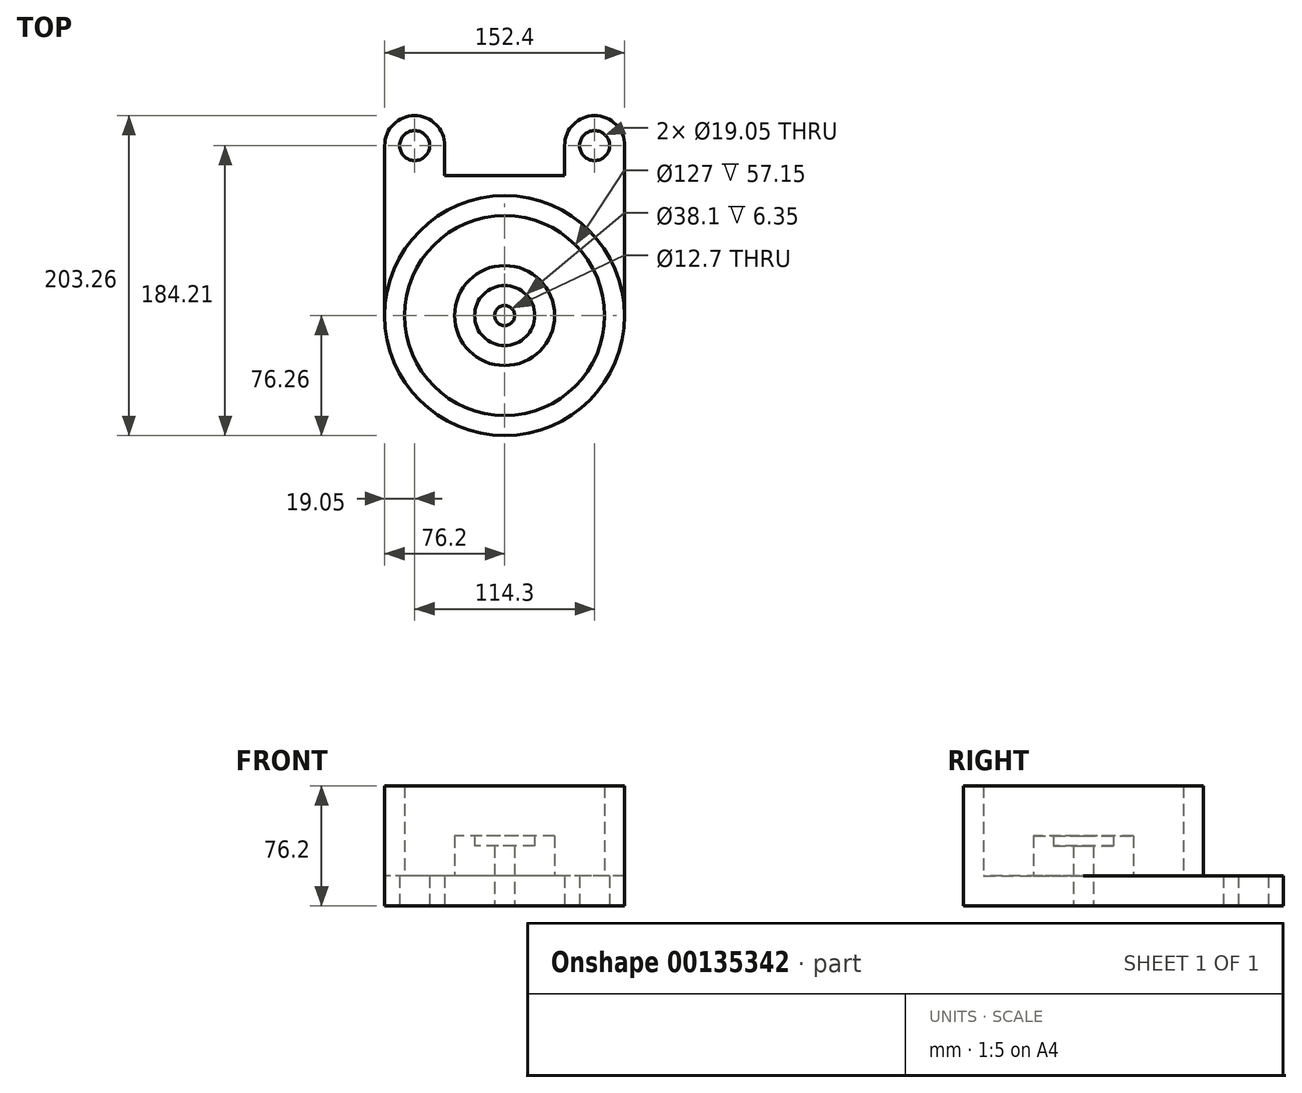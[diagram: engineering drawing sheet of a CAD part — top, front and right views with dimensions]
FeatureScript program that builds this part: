
annotation { "Feature Type Name" : "Feature", "Feature Type Description" : "" }
export const myFeature = defineFeature(function(context is Context, id is Id, definition is map)
    precondition{}
    {
        {
            var Q0;
            Q0=qCreatedBy(makeId("Top.planeOp"),FACE);
            var sketch = newSketch(context, id + "F0", { "sketchPlane" : qUnion([Q0])});
            skLineSegment(sketch, "E0", {"start": v(-76.2, 0) * mm, "end": v(0, 0) * mm, "construction": true});
            skLineSegment(sketch, "E1", {"start": v(-76.2, 0) * mm, "end": v(-76.2, 107.95) * mm});
            skArc(sketch, "E2", {"start": v(-38.1, 107.95) * mm, "mid": v(-57.15, 127) * mm, "end": v(-76.2, 107.95) * mm});
            skCircle(sketch, "E3", {"center": v(-57.15, 107.95) * mm, "radius": 9.53 * mm});
            skCircle(sketch, "E4", {"center": v(0, 0) * mm, "radius": 19.05 * mm});
            skCircle(sketch, "E5", {"center": v(0, 0) * mm, "radius": 31.75 * mm});
            skCircle(sketch, "E6", {"center": v(0, 0) * mm, "radius": 63.5 * mm});
            skCircle(sketch, "E7", {"center": v(0, -0.06) * mm, "radius": 76.2 * mm});
            skLineSegment(sketch, "E8.MirrorCS", {"start": v(-76.2, 0) * mm, "end": v(-152.4, 0) * mm, "construction": true});
            skLineSegment(sketch, "E9.MirrorCS", {"start": v(-76.2, 0) * mm, "end": v(-76.2, -107.95) * mm});
            skArc(sketch, "E10.MirrorCS", {"start": v(-38.1, -107.95) * mm, "mid": v(-57.15, -127) * mm, "end": v(-76.2, -107.95) * mm});
            skCircle(sketch, "E11.MirrorC", {"center": v(-57.15, -107.95) * mm, "radius": 9.53 * mm});
            skLineSegment(sketch, "E12", {"start": v(0, 157.5) * mm, "end": v(0, -133.46) * mm, "construction": true});
            skArc(sketch, "E13.MirrorCS", {"start": v(38.1, 107.95) * mm, "mid": v(57.15, 127) * mm, "end": v(76.2, 107.95) * mm});
            skLineSegment(sketch, "E14.MirrorCS", {"start": v(76.2, 0) * mm, "end": v(76.2, 107.95) * mm});
            skCircle(sketch, "E15.MirrorC", {"center": v(57.15, 107.95) * mm, "radius": 9.53 * mm});
            skLineSegment(sketch, "E16.MirrorCS", {"start": v(76.2, 0) * mm, "end": v(76.2, -107.95) * mm});
            skArc(sketch, "E17.MirrorCS", {"start": v(38.1, -107.95) * mm, "mid": v(57.15, -127) * mm, "end": v(76.2, -107.95) * mm});
            skCircle(sketch, "E18.MirrorC", {"center": v(57.15, -107.95) * mm, "radius": 9.53 * mm});
            skLineSegment(sketch, "E19", {"start": v(-38.1, 107.95) * mm, "end": v(-38.1, 88.9) * mm});
            skLineSegment(sketch, "E20", {"start": v(38.1, 107.95) * mm, "end": v(38.1, 88.9) * mm});
            skLineSegment(sketch, "E21", {"start": v(38.1, 88.9) * mm, "end": v(-38.1, 88.9) * mm});
            skLineSegment(sketch, "E22", {"start": v(38.1, -107.95) * mm, "end": v(38.1, -88.9) * mm});
            skLineSegment(sketch, "E23", {"start": v(38.1, -88.9) * mm, "end": v(-37.76, -88.9) * mm});
            skLineSegment(sketch, "E24", {"start": v(-37.76, -88.9) * mm, "end": v(-38.1, -107.95) * mm});
            skCircle(sketch, "E25", {"center": v(0, 0) * mm, "radius": 6.35 * mm});
            skSolve(sketch);
        }
        {
            var Q0;
            {var subQ5=sQuery(id+"F0.wireOp",EDGE,"E1");Q0=makeQuery(id+"F0.imprint","IMPRINT",FACE,{"disambiguationData":[TD([[makeQuery(id+"F0.imprint","IMPRINT",EDGE,{"derivedFrom":subQ5}),-1.0]])]});}
            var Q1;
            {var subQ0=sQuery(id+"F0.wireOp",EDGE,"E10.MirrorCS");Q1=makeQuery(id+"F0.imprint","IMPRINT",FACE,{"disambiguationData":[TD([[makeQuery(id+"F0.imprint","IMPRINT",EDGE,{"derivedFrom":subQ0}),-1.0]])]});}
            var Q2;
            Q2=makeQuery(id+"F0.imprint","IMPRINT",FACE,{"disambiguationData":[TD([[makeQuery(id+"F0.imprint","IMPRINT",EDGE,{"derivedFrom":sQuery(id+"F0.wireOp",EDGE,"E5")}),-1.0]])]});
            extrude(context, id + "F1", {"entities" : qUnion([Q0, Q1, Q2]), "depth" : 19.05 * mm});
        }
        {
            var Q0;
            Q0=makeQuery(id+"F0.imprint","IMPRINT",FACE,{"disambiguationData":[TD([[makeQuery(id+"F0.imprint","IMPRINT",EDGE,{"derivedFrom":sQuery(id+"F0.wireOp",EDGE,"E6")}),-1.0]])]});
            extrude(context, id + "F2", {"entities" : qUnion([Q0]), "operationType" : NewBodyOperationType.ADD, "depth" : 76.2 * mm});
        }
        {
            var Q0;
            Q0=makeQuery(id+"F0.imprint","IMPRINT",FACE,{"disambiguationData":[TD([[makeQuery(id+"F0.imprint","IMPRINT",EDGE,{"derivedFrom":sQuery(id+"F0.wireOp",EDGE,"E4")}),-1.0]])]});
            extrude(context, id + "F3", {"entities" : qUnion([Q0]), "operationType" : NewBodyOperationType.ADD, "depth" : 44.45 * mm});
        }
        {
            var Q0;
            Q0=makeQuery(id+"F0.imprint","IMPRINT",FACE,{"disambiguationData":[TD([[makeQuery(id+"F0.imprint","IMPRINT",EDGE,{"derivedFrom":sQuery(id+"F0.wireOp",EDGE,"E4")}),1.0]])]});
            extrude(context, id + "F4", {"entities" : qUnion([Q0]), "operationType" : NewBodyOperationType.ADD, "depth" : 38.1 * mm});
        }
    });
